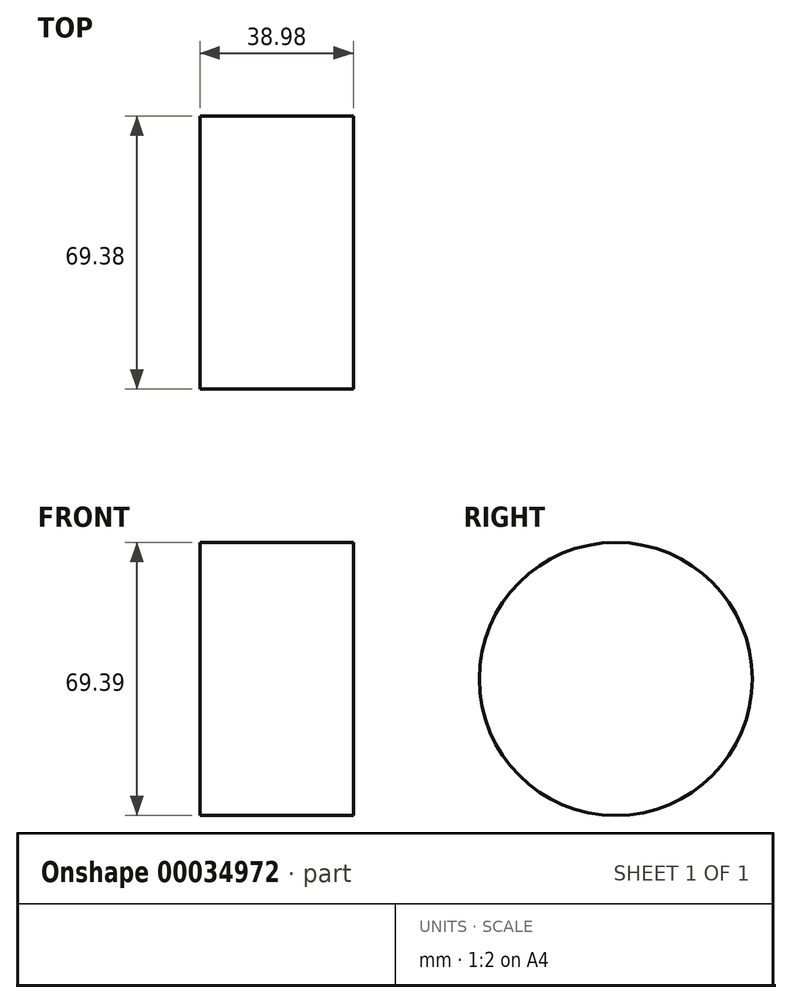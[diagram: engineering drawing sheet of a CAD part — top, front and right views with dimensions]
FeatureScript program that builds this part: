
annotation { "Feature Type Name" : "Feature", "Feature Type Description" : "" }
export const myFeature = defineFeature(function(context is Context, id is Id, definition is map)
    precondition{}
    {
        {
            var Q0;
            Q0=qCreatedBy(makeId("Front.planeOp"),FACE);
            var sketch = newSketch(context, id + "F0", { "sketchPlane" : qUnion([Q0])});
            skLineSegment(sketch, "E0.bottom", {"start": v(-152.07, 16.56) * mm, "end": v(-113.1, 16.56) * mm});
            skLineSegment(sketch, "E0.top", {"start": v(-152.07, -18.14) * mm, "end": v(-113.1, -18.14) * mm});
            skLineSegment(sketch, "E0.left", {"start": v(-152.07, 16.56) * mm, "end": v(-152.07, -18.14) * mm});
            skLineSegment(sketch, "E0.right", {"start": v(-113.1, 16.56) * mm, "end": v(-113.1, -18.14) * mm});
            skSolve(sketch);
        }
        {
            var Q0;
            Q0 = qSketchRegion(id + "F0", true);
            var Q1;
            Q1=sQuery(id+"F0.wireOp",EDGE,"E0.bottom");
            revolve(context, id + "F1", {"entities" : qUnion([Q0]), "axis" : qUnion([Q1]), "revolveType" : RevolveType.FULL});
        }
    });
